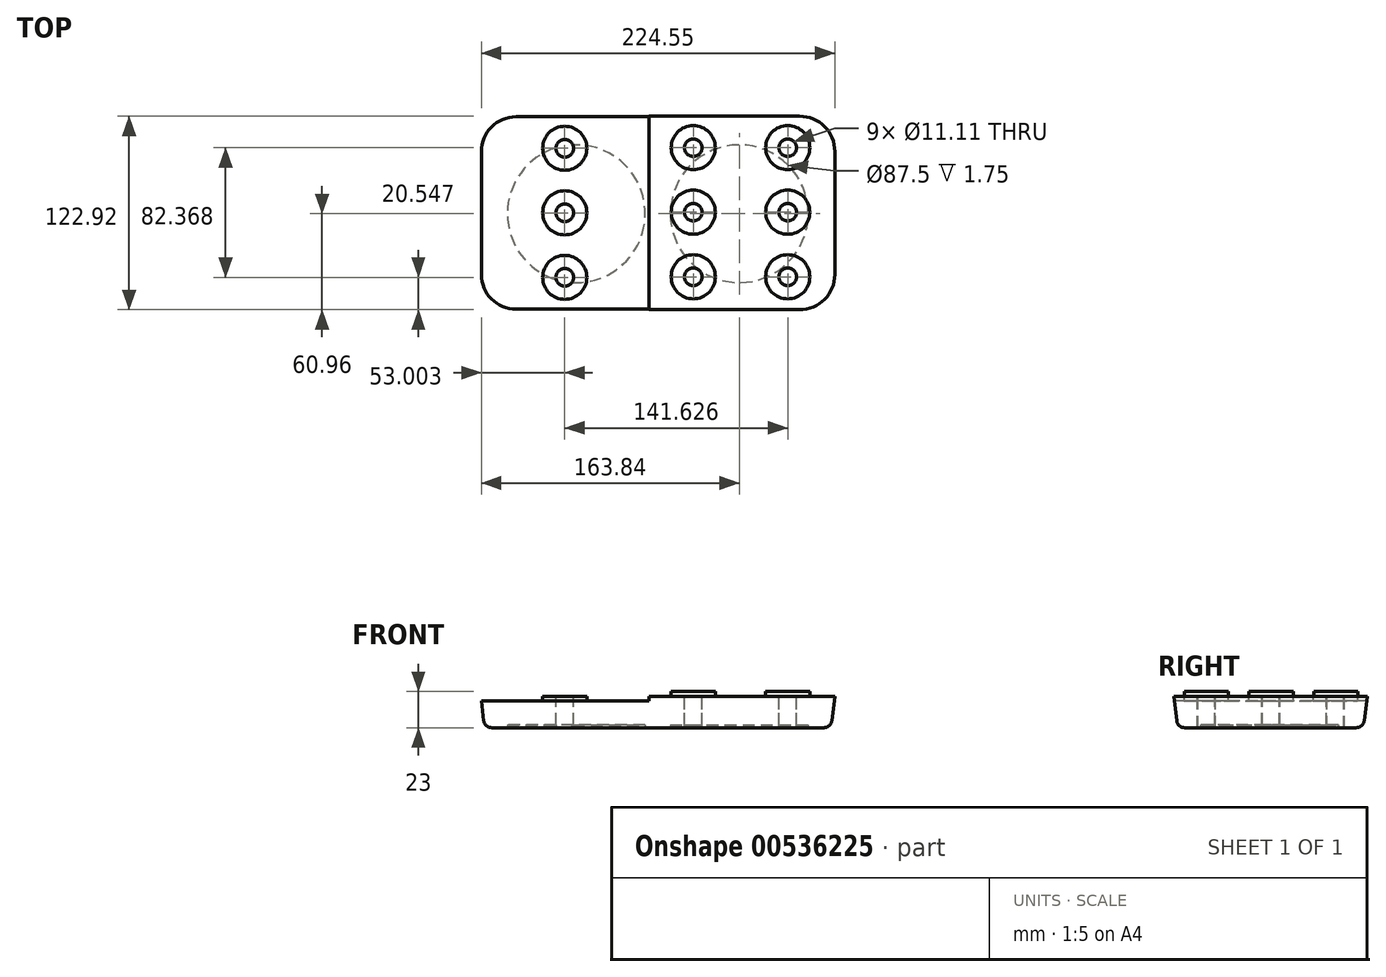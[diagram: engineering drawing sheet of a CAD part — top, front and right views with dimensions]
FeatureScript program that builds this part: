
annotation { "Feature Type Name" : "Feature", "Feature Type Description" : "" }
export const myFeature = defineFeature(function(context is Context, id is Id, definition is map)
    precondition{}
    {
        {
            var Q0;
            Q0=qCreatedBy(makeId("Top.planeOp"),FACE);
            var sketch = newSketch(context, id + "F0", { "sketchPlane" : qUnion([Q0])});
            skLineSegment(sketch, "E0.bottom", {"start": v(20, 0) * mm, "end": v(200, 0) * mm});
            skLineSegment(sketch, "E0.top", {"start": v(20, 118) * mm, "end": v(200, 118) * mm});
            skLineSegment(sketch, "E0.left", {"start": v(0, 20) * mm, "end": v(0, 98) * mm});
            skLineSegment(sketch, "E0.right", {"start": v(220, 20) * mm, "end": v(220, 98) * mm});
            skPoint(sketch, "E1.visualSharp", {"position": v(0, 118) * mm});
            skArc(sketch, "E1.filletArc", {"start": v(20, 118) * mm, "mid": v(5.86, 112.14) * mm, "end": v(0, 98) * mm});
            skPoint(sketch, "E2.visualSharp", {"position": v(220, 118) * mm});
            skArc(sketch, "E2.filletArc", {"start": v(220, 98) * mm, "mid": v(214.14, 112.14) * mm, "end": v(200, 118) * mm});
            skPoint(sketch, "E3.visualSharp", {"position": v(0, 0) * mm});
            skArc(sketch, "E3.filletArc", {"start": v(0, 20) * mm, "mid": v(5.86, 5.86) * mm, "end": v(20, 0) * mm});
            skPoint(sketch, "E4.visualSharp", {"position": v(220, 0) * mm});
            skArc(sketch, "E4.filletArc", {"start": v(200, 0) * mm, "mid": v(214.14, 5.86) * mm, "end": v(220, 20) * mm});
            skSolve(sketch);
        }
        {
            var Q0;
            Q0=makeQuery(id+"F0.imprint","IMPRINT",FACE,{"disambiguationData":[TD([[makeQuery(id+"F0.imprint","IMPRINT",EDGE,{"derivedFrom":sQuery(id+"F0.wireOp",EDGE,"E0.bottom")}),1.0]])]});
            extrude(context, id + "F1", {"entities" : qUnion([Q0]), "depth" : 20 * mm, "hasDraft" : true, "draftAngle" : 7 * degree, "offsetDistance" : 25 * mm});
        }
        {
            var Q0;
            Q0=makeQuery(id+"F1.opExtrude","CAP_FACE",FACE,{"disambiguationData":[OSD([sQuery(id+"F0.wireOp",EDGE,"E0.bottom"),sQuery(id+"F0.wireOp",EDGE,"E0.top"),sQuery(id+"F0.wireOp",EDGE,"E0.left"),sQuery(id+"F0.wireOp",EDGE,"E0.right"),sQuery(id+"F0.wireOp",EDGE,"E1.filletArc"),sQuery(id+"F0.wireOp",EDGE,"E2.filletArc"),sQuery(id+"F0.wireOp",EDGE,"E3.filletArc"),sQuery(id+"F0.wireOp",EDGE,"E4.filletArc")])],"isStart":true});
            fillet(context, id + "F2", {"entities" : qUnion([Q0]), "radius" : 5 * mm, "tangentPropagation" : true, "allowEdgeOverflow" : false});
        }
        {
            var Q0;
            Q0=makeQuery(id+"F1.opExtrude","CAP_FACE",FACE,{"disambiguationData":[OSD([sQuery(id+"F0.wireOp",EDGE,"E0.bottom"),sQuery(id+"F0.wireOp",EDGE,"E0.top"),sQuery(id+"F0.wireOp",EDGE,"E0.left"),sQuery(id+"F0.wireOp",EDGE,"E0.right"),sQuery(id+"F0.wireOp",EDGE,"E1.filletArc"),sQuery(id+"F0.wireOp",EDGE,"E2.filletArc"),sQuery(id+"F0.wireOp",EDGE,"E3.filletArc"),sQuery(id+"F0.wireOp",EDGE,"E4.filletArc")])],"isStart":true});
            var sketch = newSketch(context, id + "F3", { "sketchPlane" : qUnion([Q0])});
            skLineSegment(sketch, "E5.bottom", {"start": v(0, 0) * mm, "end": v(58.25, 0) * mm, "construction": true});
            skLineSegment(sketch, "E5.top", {"start": v(0, -58.5) * mm, "end": v(58.25, -58.5) * mm, "construction": true});
            skLineSegment(sketch, "E5.left", {"start": v(0, 0) * mm, "end": v(0, -58.5) * mm, "construction": true});
            skLineSegment(sketch, "E5.right", {"start": v(58.25, 0) * mm, "end": v(58.25, -58.5) * mm, "construction": true});
            skLineSegment(sketch, "E6.bottom", {"start": v(0, 0) * mm, "end": v(161.75, 0) * mm, "construction": true});
            skLineSegment(sketch, "E6.top", {"start": v(0, -58.5) * mm, "end": v(161.75, -58.5) * mm, "construction": true});
            skLineSegment(sketch, "E6.right", {"start": v(161.75, 0) * mm, "end": v(161.75, -58.5) * mm, "construction": true});
            skCircle(sketch, "E7", {"center": v(58.25, -58.5) * mm, "radius": 43.75 * mm});
            skCircle(sketch, "E8", {"center": v(161.75, -58.5) * mm, "radius": 43.75 * mm});
            skSolve(sketch);
        }
        {
            var Q0;
            Q0=qSketchRegion(id+"F3",true);
            extrude(context, id + "F4", {"entities" : qUnion([Q0]), "operationType" : NewBodyOperationType.REMOVE, "oppositeDirection" : true, "depth" : 1.75 * mm});
        }
        {
            var Q0;
            Q0=makeQuery(id+"F1.opExtrude","CAP_FACE",FACE,{"disambiguationData":[OSD([sQuery(id+"F0.wireOp",EDGE,"E0.bottom"),sQuery(id+"F0.wireOp",EDGE,"E0.top"),sQuery(id+"F0.wireOp",EDGE,"E0.left"),sQuery(id+"F0.wireOp",EDGE,"E0.right"),sQuery(id+"F0.wireOp",EDGE,"E1.filletArc"),sQuery(id+"F0.wireOp",EDGE,"E2.filletArc"),sQuery(id+"F0.wireOp",EDGE,"E3.filletArc"),sQuery(id+"F0.wireOp",EDGE,"E4.filletArc")])],"isStart":false});
            var sketch = newSketch(context, id + "F5", { "sketchPlane" : qUnion([Q0])});
            skCircle(sketch, "E9", {"center": v(192.54, 100.46) * mm, "radius": 14 * mm});
            skCircle(sketch, "E10.0.1.0", {"center": v(192.54, 59.46) * mm, "radius": 14 * mm});
            skCircle(sketch, "E10.0.2.0", {"center": v(192.54, 18.46) * mm, "radius": 14 * mm});
            skCircle(sketch, "E10.1.0.0", {"center": v(132.54, 100.46) * mm, "radius": 14 * mm});
            skCircle(sketch, "E10.1.1.0", {"center": v(132.54, 59.46) * mm, "radius": 14 * mm});
            skCircle(sketch, "E10.1.2.0", {"center": v(132.54, 18.46) * mm, "radius": 14 * mm});
            skLineSegment(sketch, "E10.direction1", {"start": v(192.54, 100.46) * mm, "end": v(132.54, 100.46) * mm, "construction": true});
            skLineSegment(sketch, "E10.direction2", {"start": v(192.54, 100.46) * mm, "end": v(192.54, 59.46) * mm, "construction": true});
            skSolve(sketch);
        }
        {
            var Q0;
            Q0 = qSketchRegion(id + "F5", true);
            extrude(context, id + "F6", {"entities" : qUnion([Q0]), "operationType" : NewBodyOperationType.ADD, "depth" : 3 * mm, "offsetDistance" : 25 * mm});
        }
        {
            var Q0;
            Q0=makeQuery(id+"F6.opExtrude","CAP_FACE",FACE,{"disambiguationData":[OSD([sQuery(id+"F5.wireOp",EDGE,"E10.1.1.0")])],"isStart":false});
            var sketch = newSketch(context, id + "F7", { "sketchPlane" : qUnion([Q0])});
            skCircle(sketch, "E11", {"center": v(132.54, 100.46) * mm, "radius": 5.56 * mm});
            skCircle(sketch, "E12", {"center": v(192.54, 100.46) * mm, "radius": 5.56 * mm});
            skCircle(sketch, "E13", {"center": v(192.54, 59.46) * mm, "radius": 5.56 * mm});
            skCircle(sketch, "E14", {"center": v(132.54, 59.46) * mm, "radius": 5.56 * mm});
            skCircle(sketch, "E15", {"center": v(132.54, 18.46) * mm, "radius": 5.56 * mm});
            skCircle(sketch, "E16", {"center": v(192.54, 18.46) * mm, "radius": 5.56 * mm});
            skSolve(sketch);
        }
        {
            var Q0;
            Q0 = qSketchRegion(id + "F7", true);
            extrude(context, id + "F8", {"entities" : qUnion([Q0]), "operationType" : NewBodyOperationType.REMOVE, "endBound" : BoundingType.THROUGH_ALL, "oppositeDirection" : true, "depth" : 25 * mm, "offsetDistance" : 25 * mm});
        }
        {
            var Q0;
            Q0=makeQuery(id+"F5.imprint","IMPRINT",FACE,{"disambiguationData":[TD([[makeQuery(id+"F5.imprint","IMPRINT",EDGE,{"derivedFrom":sQuery(id+"F5.wireOp",EDGE,"E9")}),-1.0]])]});
            var sketch = newSketch(context, id + "F9", { "sketchPlane" : qUnion([Q0])});
            skLineSegment(sketch, "E17.0", {"start": v(20, 120.46) * mm, "end": v(104.54, 120.46) * mm});
            skArc(sketch, "E18.0", {"start": v(20, 120.46) * mm, "mid": v(4.12, 113.88) * mm, "end": v(-2.46, 98) * mm});
            skLineSegment(sketch, "E19.0", {"start": v(-2.46, 20) * mm, "end": v(-2.46, 98) * mm});
            skArc(sketch, "E20.0", {"start": v(-2.46, 20) * mm, "mid": v(4.12, 4.12) * mm, "end": v(20, -2.46) * mm});
            skLineSegment(sketch, "E21.0", {"start": v(20, -2.46) * mm, "end": v(104.54, -2.46) * mm});
            skLineSegment(sketch, "E22", {"start": v(104.54, 120.46) * mm, "end": v(104.54, -2.46) * mm});
            skSolve(sketch);
        }
        {
            var Q0;
            Q0 = qSketchRegion(id + "F9", true);
            extrude(context, id + "F10", {"entities" : qUnion([Q0]), "operationType" : NewBodyOperationType.REMOVE, "oppositeDirection" : true, "depth" : 3 * mm, "offsetDistance" : 25 * mm});
        }
        {
            var Q0;
            Q0=makeQuery(id+"F10.boolean.opBoolean","COPY",FACE,{"derivedFrom":makeQuery(id+"F10.opExtrude","CAP_FACE",FACE,{"disambiguationData":[OSD([sQuery(id+"F9.wireOp",EDGE,"E17.0"),sQuery(id+"F9.wireOp",EDGE,"E18.0"),sQuery(id+"F9.wireOp",EDGE,"E19.0"),sQuery(id+"F9.wireOp",EDGE,"E20.0"),sQuery(id+"F9.wireOp",EDGE,"E21.0"),sQuery(id+"F9.wireOp",EDGE,"E22")])],"isStart":false})});
            var sketch = newSketch(context, id + "F11", { "sketchPlane" : qUnion([Q0])});
            skCircle(sketch, "E23", {"center": v(50.91, 100.09) * mm, "radius": 14 * mm});
            skCircle(sketch, "E24.0.1.0", {"center": v(50.91, 59.09) * mm, "radius": 14 * mm});
            skCircle(sketch, "E24.0.2.0", {"center": v(50.91, 18.09) * mm, "radius": 14 * mm});
            skLineSegment(sketch, "E24.direction1", {"start": v(50.91, 100.09) * mm, "end": v(75.68, 100.09) * mm, "construction": true});
            skLineSegment(sketch, "E24.direction2", {"start": v(50.91, 100.09) * mm, "end": v(50.91, 59.09) * mm, "construction": true});
            skSolve(sketch);
        }
        {
            var Q0;
            Q0 = qSketchRegion(id + "F11", true);
            extrude(context, id + "F12", {"entities" : qUnion([Q0]), "operationType" : NewBodyOperationType.ADD, "depth" : 3 * mm, "offsetDistance" : 25 * mm});
        }
        {
            var Q0;
            Q0=makeQuery(id+"F5.imprint","IMPRINT",FACE,{"disambiguationData":[TD([[makeQuery(id+"F5.imprint","IMPRINT",EDGE,{"derivedFrom":sQuery(id+"F5.wireOp",EDGE,"E9")}),-1.0]])]});
            var sketch = newSketch(context, id + "F13", { "sketchPlane" : qUnion([Q0])});
            skCircle(sketch, "E25", {"center": v(50.91, 100.09) * mm, "radius": 5.56 * mm});
            skCircle(sketch, "E26", {"center": v(50.91, 59.09) * mm, "radius": 5.56 * mm});
            skCircle(sketch, "E27", {"center": v(50.91, 18.09) * mm, "radius": 5.56 * mm});
            skSolve(sketch);
        }
        {
            var Q0;
            Q0 = qSketchRegion(id + "F13", true);
            extrude(context, id + "F14", {"entities" : qUnion([Q0]), "operationType" : NewBodyOperationType.REMOVE, "endBound" : BoundingType.THROUGH_ALL, "oppositeDirection" : true, "depth" : 25 * mm, "offsetDistance" : 25 * mm});
        }
    });
